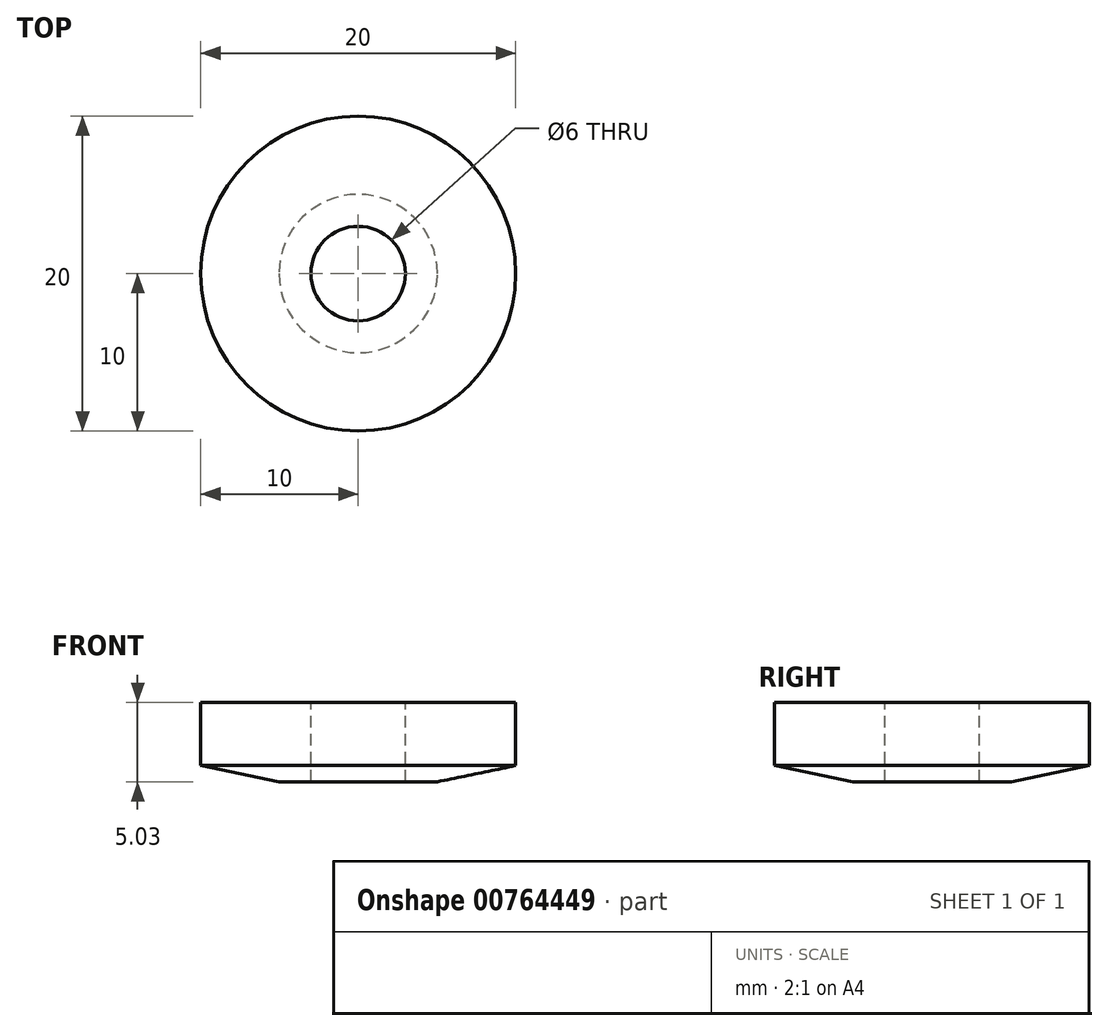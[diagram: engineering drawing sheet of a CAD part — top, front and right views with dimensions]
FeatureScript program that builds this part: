
annotation { "Feature Type Name" : "Feature", "Feature Type Description" : "" }
export const myFeature = defineFeature(function(context is Context, id is Id, definition is map)
    precondition{}
    {
        {
            var Q0;
            Q0=qCreatedBy(makeId("Right.planeOp"),FACE);
            var sketch = newSketch(context, id + "F0", { "sketchPlane" : qUnion([Q0])});
            skLineSegment(sketch, "E0", {"start": v(10, -1.49) * mm, "end": v(10, 2.52) * mm});
            skLineSegment(sketch, "E1", {"start": v(10, 2.52) * mm, "end": v(0, 2.52) * mm});
            skLineSegment(sketch, "E2", {"start": v(0, 2.52) * mm, "end": v(0, -2.51) * mm});
            skLineSegment(sketch, "E3", {"start": v(0, -2.51) * mm, "end": v(5.03, -2.51) * mm});
            skLineSegment(sketch, "E4", {"start": v(5.03, -2.51) * mm, "end": v(10, -1.49) * mm});
            skSolve(sketch);
        }
        {
            var Q0;
            Q0 = qSketchRegion(id + "F0", true);
            var Q1;
            Q1=sQuery(id+"F0.wireOp",EDGE,"E2");
            revolve(context, id + "F1", {"surfaceOperationType" : NewSurfaceOperationType.NEW, "entities" : qUnion([Q0]), "axis" : qUnion([Q1]), "revolveType" : RevolveType.FULL});
        }
        {
            var Q0;
            Q0=qCreatedBy(makeId("Top.planeOp"),FACE);
            var sketch = newSketch(context, id + "F2", { "sketchPlane" : qUnion([Q0])});
            skCircle(sketch, "E5", {"center": v(0, 0) * mm, "radius": 3 * mm});
            skSolve(sketch);
        }
        {
            var Q0;
            Q0 = qSketchRegion(id + "F2", true);
            extrude(context, id + "F3", {"entities" : qUnion([Q0]), "operationType" : NewBodyOperationType.REMOVE, "endBound" : BoundingType.SYMMETRIC, "oppositeDirection" : true, "depth" : 25 * mm, "offsetDistance" : 25 * mm});
        }
    });
